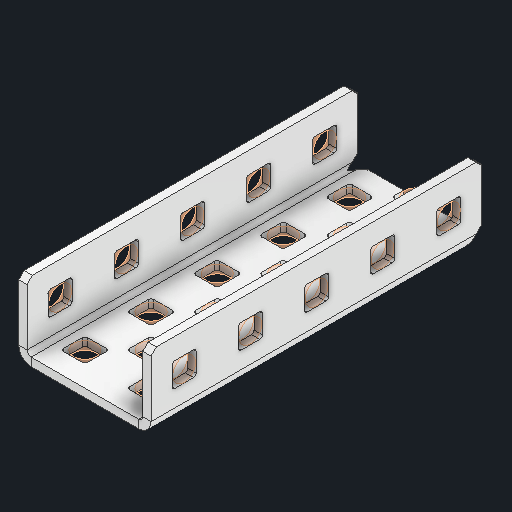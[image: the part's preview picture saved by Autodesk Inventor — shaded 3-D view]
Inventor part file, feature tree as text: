
AUTODESK INVENTOR PART (.ipt)
format: ipt  version: 2024 (Build 280153000, 153)  size: 580,096 bytes
history: native  units: in
note: dims shown in document units (in); Inventor stores cm internally (conversion verified against a paired STEP export)
features: other x32, extrude x23, sheet_metal_op x11, pattern_linear x2, mirror x1, chamfer x1, sketch x1
ambient origin geometry x8: Origin, YZ Plane, XZ Plane, XY Plane, X Axis, Y Axis, Z Axis, Center Point
bodies: Solid1 (feature_tree), Body (feature_tree)
feature tree (71):
  sheet_metal_op  "Flanges"
  other  "Flange Pattern Plane"
  other  "Flange Pattern Sketch"
  sheet_metal_op  "Flange Pattern"
  sheet_metal_op  "Body Pattern"
  pattern_linear  "Center Pattern"  Spacing1=2.5in  [1 undecoded]
  other  "Arc Length"
  mirror  "Notch Mirror"
  pattern_linear  "Notch Pattern"  Spacing1=0.0625in  [1 undecoded]
  chamfer  "End Chamfer"
  extrude  "Half Cut"  Depth=0.0625in
  other  "Plate1"
  sketch  "Sketch2"  dims[d0=1.0in d1=2.5in d2=0.0625in d3=0.0625in d4=0.0312in d5=0.125in d6=0.0625in d7=0.5in d8=90.0deg d9=0.0312in d10=0.25in d11=0.0625in d12=0.0625in d16=0.182in d17=0.02in d18=0.0625in d19=0.0in d20=0.25in d21=0.25in d38=1.9685in d40=0.5in d41=0.7874in d43=1.0in d46=0.172in d47=1.0in d48=0.0in d49=0.182in d50=0.02in d51=0.25in d52=0.25in d53=0.0625in d54=0.0in d55=0.172in d56=1.0in d57=0.0in d58=0.25in d60=1.9685in d62=0.5in d63=0.7874in d65=0.5in d85=0.1473in d86=0.1782in d88=0.04in d89=0.0625in d90=0.0in d91=0.04in d92=0.0491in d95=2.5in d96=0.04in d97=0.25in d98=45.0deg d99=0.25in d100=0.5in d101=0.0in d102=2.497in d106=0.182in d107=0.02in d108=0.5in d109=0.5in d110=0.0625in d111=0.0in d112=0.172in d113=0.5in d114=0.0in d117=0.5in d118=0.5in d119=0.5in]
  other  "Plate2"
  sheet_metal_op  "Bend1"
  sheet_metal_op  "Corner1"
  other  "Srf1"
  other  "Srf2"
  other  "Srf91"
  sheet_metal_op  "Body Pattern Sketch"
  other  "Srf92"
  other  "Srf786"
  other  "Srf823"
  other  "Srf824"
  other  "Srf825"
  other  "Srf826"
  other  "Srf827"
  other  "Srf828"
  other  "Srf829"
  other  "Srf856"
  other  "Srf857"
  other  "Srf858"
  other  "Srf859"
  other  "Srf860"
  other  "Srf861"
  other  "Srf862"
  other  "Srf889"
  other  "Srf890"
  other  "Srf891"
  other  "Srf892"
  other  "Srf922"
  other  "Srf959"
  sheet_metal_op  "Flange Stamp"
  sheet_metal_op  "Flange Circle"
  sheet_metal_op  "Body Stamp"
  sheet_metal_op  "Body Circle"
  other  "Center Stamp"
  other  "Center Circle"
  sheet_metal_op  "Notch"
  extrude  "ExtrusionSrf2"  Depth=0.0312in
  extrude  "ExtrusionSrf92"  Depth=0.5in
  extrude  "ExtrusionSrf823"  Depth=0.0625in
  extrude  "ExtrusionSrf824"  Depth=0.5in TaperAngle=90.0deg
  extrude  "ExtrusionSrf825"  Depth=0.5in
  extrude  "ExtrusionSrf826"  Depth=0.0625in
  extrude  "ExtrusionSrf827"  Depth=0.0625in
  extrude  "ExtrusionSrf828"  Depth=0.5in
  extrude  "ExtrusionSrf829"  Depth=0.02in
  extrude  "ExtrusionSrf856"  Depth=0.0625in
  extrude  "ExtrusionSrf857"  TaperAngle=0.0deg  [1 undecoded]
  extrude  "ExtrusionSrf858"  Depth=0.5in
  extrude  "ExtrusionSrf859"  Depth=0.5in
  extrude  "ExtrusionSrf860"  Depth=0.5in
  extrude  "ExtrusionSrf861"  Depth=0.5in
  extrude  "ExtrusionSrf862"  Depth=1.0in TaperAngle=0.0deg
  extrude  "ExtrusionSrf889"  Depth=0.5in
  extrude  "ExtrusionSrf890"  Depth=0.02in
  extrude  "ExtrusionSrf891"  Depth=0.5in
  extrude  "ExtrusionSrf892"  Depth=0.5in
  extrude  "ExtrusionSrf922"  Depth=0.0625in
  extrude  "ExtrusionSrf959"  TaperAngle=0.0deg  [1 undecoded]
note: 4 required parameter values undecoded (feature->parameter linkage not recoverable at this tier; creation-order binding heuristic only, values carry confidence <= 0.55)
